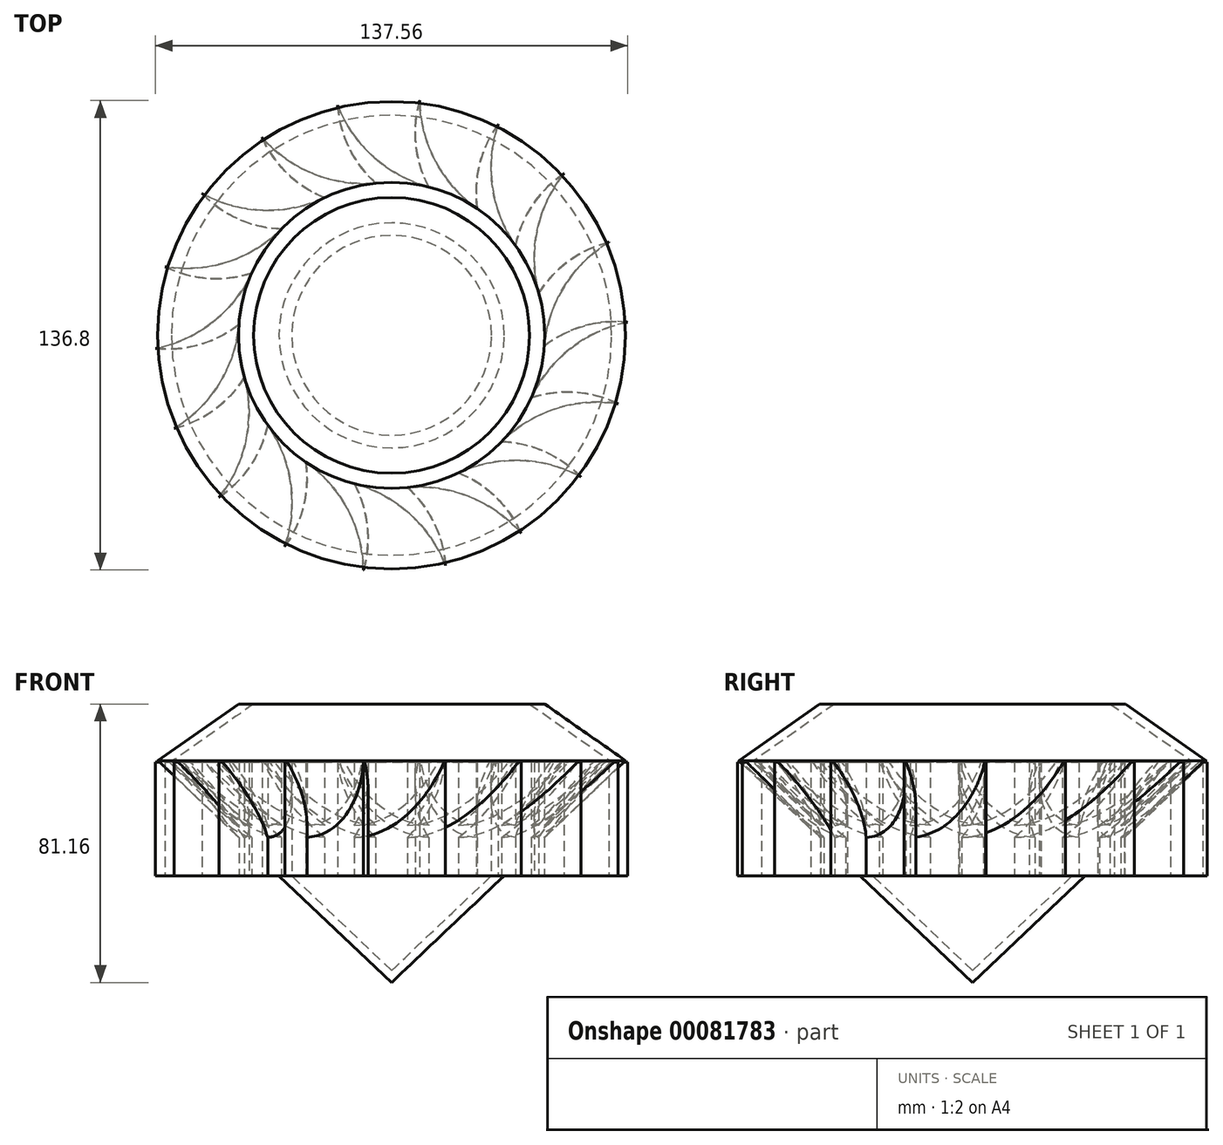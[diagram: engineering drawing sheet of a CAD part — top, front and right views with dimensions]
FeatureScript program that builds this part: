
annotation { "Feature Type Name" : "Feature", "Feature Type Description" : "" }
export const myFeature = defineFeature(function(context is Context, id is Id, definition is map)
    precondition{}
    {
        {
            var Q0;
            Q0=qCreatedBy(makeId("Front.planeOp"),FACE);
            var sketch = newSketch(context, id + "F0", { "sketchPlane" : qUnion([Q0])});
            skLineSegment(sketch, "E0", {"start": v(0, -47.69) * mm, "end": v(-68.1, 16.93) * mm});
            skLineSegment(sketch, "E1", {"start": v(-68.1, 16.93) * mm, "end": v(-44.59, 33.47) * mm});
            skLineSegment(sketch, "E2", {"start": v(-44.59, 33.47) * mm, "end": v(0, 33.47) * mm});
            skLineSegment(sketch, "E3", {"start": v(-68.1, 16.93) * mm, "end": v(0, 16.93) * mm});
            skLineSegment(sketch, "E4.MirrorCS", {"start": v(68.1, 16.93) * mm, "end": v(0, 16.93) * mm});
            skLineSegment(sketch, "E5.MirrorCS", {"start": v(44.59, 33.47) * mm, "end": v(0, 33.47) * mm});
            skLineSegment(sketch, "E6.MirrorCS", {"start": v(68.1, 16.93) * mm, "end": v(44.59, 33.47) * mm});
            skLineSegment(sketch, "E7.MirrorCS", {"start": v(0, -47.69) * mm, "end": v(68.1, 16.93) * mm});
            skLineSegment(sketch, "E8", {"start": v(0, 33.47) * mm, "end": v(0, -50.76) * mm});
            skSolve(sketch);
        }
        {
            var Q0;
            Q0=makeQuery(id+"F0.imprint","IMPRINT",FACE,{"disambiguationData":[TD([[makeQuery(id+"F0.imprint","IMPRINT",EDGE,{"derivedFrom":sQuery(id+"F0.wireOp",EDGE,"E1")}),-1.0]])]});
            var Q1;
            {var subQ0=sQuery(id+"F0.wireOp",EDGE,"E0");Q1=makeQuery(id+"F0.imprint","IMPRINT",FACE,{"disambiguationData":[TD([[makeQuery(id+"F0.imprint","IMPRINT",EDGE,{"derivedFrom":subQ0}),-1.0]])]});}
            var Q2;
            Q2=sQuery(id+"F0.wireOp",EDGE,"E8");
            revolve(context, id + "F1", {"entities" : qUnion([Q0, Q1]), "axis" : qUnion([Q2]), "revolveType" : RevolveType.FULL});
        }
        {
            var Q0;
            Q0=makeQuery(id+"F1.opRevolve","SWEPT_FACE",FACE,{"disambiguationData":[OSD([sQuery(id+"F0.wireOp",EDGE,"E2")])]});
            var Q1;
            Q1=makeQuery(id+"F1.opRevolve","SWEPT_BODY",BODY,{"disambiguationData":[OSD([sQuery(id+"F0.wireOp",EDGE,"E0"),sQuery(id+"F0.wireOp",EDGE,"E1"),sQuery(id+"F0.wireOp",EDGE,"E2"),sQuery(id+"F0.wireOp",EDGE,"E8")])]});
            shell(context, id + "F2", {"entities" : qUnion([Q0]), "parts" : qUnion([Q1]), "thickness" : 2.54 * mm});
        }
        {
            var Q0;
            Q0=qCreatedBy(makeId("Top.planeOp"),FACE);
            var sketch = newSketch(context, id + "F3", { "sketchPlane" : qUnion([Q0])});
            skLineSegment(sketch, "E9", {"start": v(0, 40.18) * mm, "end": v(-4.62, 44.33) * mm});
            skLineSegment(sketch, "E10.1.0", {"start": v(-13.74, 37.76) * mm, "end": v(-19.5, 40.08) * mm});
            skLineSegment(sketch, "E10.2.0", {"start": v(-25.83, 30.78) * mm, "end": v(-32.03, 31) * mm});
            skPoint(sketch, "E10.center", {"position": v(0, 0) * mm});
            skLineSegment(sketch, "E11.2.3.0", {"start": v(-34.8, 20.09) * mm, "end": v(-40.7, 18.17) * mm});
            skLineSegment(sketch, "E11.2.4.0", {"start": v(-39.57, 6.98) * mm, "end": v(-44.46, 3.15) * mm});
            skLineSegment(sketch, "E11.2.5.0", {"start": v(-39.57, -6.98) * mm, "end": v(-42.86, -12.25) * mm});
            skLineSegment(sketch, "E11.2.6.0", {"start": v(-34.8, -20.09) * mm, "end": v(-36.08, -26.16) * mm});
            skLineSegment(sketch, "E11.2.7.0", {"start": v(-25.83, -30.78) * mm, "end": v(-24.96, -36.93) * mm});
            skLineSegment(sketch, "E11.2.8.0", {"start": v(-13.74, -37.76) * mm, "end": v(-10.82, -43.24) * mm});
            skLineSegment(sketch, "E11.2.9.0", {"start": v(0, -40.18) * mm, "end": v(4.62, -44.33) * mm});
            skLineSegment(sketch, "E11.2.10.0", {"start": v(13.74, -37.76) * mm, "end": v(19.5, -40.08) * mm});
            skLineSegment(sketch, "E11.2.11.0", {"start": v(25.83, -30.78) * mm, "end": v(32.03, -31) * mm});
            skLineSegment(sketch, "E11.2.12.0", {"start": v(34.8, -20.09) * mm, "end": v(40.7, -18.17) * mm});
            skLineSegment(sketch, "E11.2.13.0", {"start": v(39.57, -6.98) * mm, "end": v(44.46, -3.15) * mm});
            skLineSegment(sketch, "E11.2.14.0", {"start": v(39.57, 6.98) * mm, "end": v(42.86, 12.25) * mm});
            skLineSegment(sketch, "E11.2.15.0", {"start": v(34.8, 20.09) * mm, "end": v(36.08, 26.16) * mm});
            skLineSegment(sketch, "E11.2.16.0", {"start": v(25.83, 30.78) * mm, "end": v(24.96, 36.93) * mm});
            skLineSegment(sketch, "E11.2.17.0", {"start": v(13.74, 37.76) * mm, "end": v(10.82, 43.24) * mm});
            skArc(sketch, "E12", {"start": v(-37.7, 57.65) * mm, "mid": v(-22.75, 47.05) * mm, "end": v(-4.62, 44.33) * mm});
            skArc(sketch, "E13", {"start": v(-37.7, 57.65) * mm, "mid": v(-30.31, 47.1) * mm, "end": v(-19.5, 40.08) * mm});
            skArc(sketch, "E14.1.0", {"start": v(-55.15, 41.27) * mm, "mid": v(-44.6, 33.88) * mm, "end": v(-32.03, 31) * mm});
            skArc(sketch, "E14.1.1", {"start": v(-55.15, 41.27) * mm, "mid": v(-37.47, 36.43) * mm, "end": v(-19.5, 40.08) * mm});
            skArc(sketch, "E14.2.0", {"start": v(-65.94, 19.92) * mm, "mid": v(-53.5, 16.59) * mm, "end": v(-40.7, 18.17) * mm});
            skArc(sketch, "E14.2.1", {"start": v(-65.94, 19.92) * mm, "mid": v(-47.67, 21.42) * mm, "end": v(-32.03, 31) * mm});
            skArc(sketch, "E15.2.3.0", {"start": v(-68.78, -3.83) * mm, "mid": v(-55.94, -2.7) * mm, "end": v(-44.46, 3.15) * mm});
            skArc(sketch, "E15.4.3.0", {"start": v(-68.78, -3.83) * mm, "mid": v(-52.12, 3.83) * mm, "end": v(-40.7, 18.17) * mm});
            skArc(sketch, "E15.2.4.0", {"start": v(-63.32, -27.12) * mm, "mid": v(-51.64, -21.68) * mm, "end": v(-42.86, -12.25) * mm});
            skArc(sketch, "E15.4.4.0", {"start": v(-63.32, -27.12) * mm, "mid": v(-50.29, -14.23) * mm, "end": v(-44.46, 3.15) * mm});
            skArc(sketch, "E15.2.5.0", {"start": v(-50.22, -47.14) * mm, "mid": v(-41.11, -38.03) * mm, "end": v(-36.08, -26.16) * mm});
            skArc(sketch, "E15.4.5.0", {"start": v(-50.22, -47.14) * mm, "mid": v(-42.39, -30.57) * mm, "end": v(-42.86, -12.25) * mm});
            skArc(sketch, "E15.2.6.0", {"start": v(-31.07, -61.48) * mm, "mid": v(-25.62, -49.8) * mm, "end": v(-24.96, -36.93) * mm});
            skArc(sketch, "E15.4.6.0", {"start": v(-31.07, -61.48) * mm, "mid": v(-29.37, -43.22) * mm, "end": v(-36.08, -26.16) * mm});
            skArc(sketch, "E15.2.7.0", {"start": v(-8.17, -68.4) * mm, "mid": v(-7.05, -55.56) * mm, "end": v(-10.82, -43.24) * mm});
            skArc(sketch, "E15.4.7.0", {"start": v(-8.17, -68.4) * mm, "mid": v(-12.82, -50.66) * mm, "end": v(-24.96, -36.93) * mm});
            skArc(sketch, "E15.2.8.0", {"start": v(15.72, -67.07) * mm, "mid": v(12.38, -54.62) * mm, "end": v(4.62, -44.33) * mm});
            skArc(sketch, "E15.4.8.0", {"start": v(15.72, -67.07) * mm, "mid": v(5.28, -52) * mm, "end": v(-10.82, -43.24) * mm});
            skArc(sketch, "E15.2.9.0", {"start": v(37.7, -57.65) * mm, "mid": v(30.31, -47.1) * mm, "end": v(19.5, -40.08) * mm});
            skArc(sketch, "E15.4.9.0", {"start": v(37.7, -57.65) * mm, "mid": v(22.75, -47.05) * mm, "end": v(4.62, -44.33) * mm});
            skArc(sketch, "E15.2.10.0", {"start": v(55.15, -41.27) * mm, "mid": v(44.6, -33.88) * mm, "end": v(32.03, -31) * mm});
            skArc(sketch, "E15.4.10.0", {"start": v(55.15, -41.27) * mm, "mid": v(37.47, -36.43) * mm, "end": v(19.5, -40.08) * mm});
            skArc(sketch, "E15.2.11.0", {"start": v(65.94, -19.92) * mm, "mid": v(53.5, -16.59) * mm, "end": v(40.7, -18.17) * mm});
            skArc(sketch, "E15.4.11.0", {"start": v(65.94, -19.92) * mm, "mid": v(47.67, -21.42) * mm, "end": v(32.03, -31) * mm});
            skArc(sketch, "E15.2.12.0", {"start": v(68.78, 3.83) * mm, "mid": v(55.94, 2.7) * mm, "end": v(44.46, -3.15) * mm});
            skArc(sketch, "E15.4.12.0", {"start": v(68.78, 3.83) * mm, "mid": v(52.12, -3.83) * mm, "end": v(40.7, -18.17) * mm});
            skArc(sketch, "E15.2.13.0", {"start": v(63.32, 27.12) * mm, "mid": v(51.64, 21.68) * mm, "end": v(42.86, 12.25) * mm});
            skArc(sketch, "E15.4.13.0", {"start": v(63.32, 27.12) * mm, "mid": v(50.29, 14.23) * mm, "end": v(44.46, -3.15) * mm});
            skArc(sketch, "E15.2.14.0", {"start": v(50.22, 47.14) * mm, "mid": v(41.11, 38.03) * mm, "end": v(36.08, 26.16) * mm});
            skArc(sketch, "E15.4.14.0", {"start": v(50.22, 47.14) * mm, "mid": v(42.39, 30.57) * mm, "end": v(42.86, 12.25) * mm});
            skArc(sketch, "E15.2.15.0", {"start": v(31.07, 61.48) * mm, "mid": v(25.62, 49.8) * mm, "end": v(24.96, 36.93) * mm});
            skArc(sketch, "E15.4.15.0", {"start": v(31.07, 61.48) * mm, "mid": v(29.37, 43.22) * mm, "end": v(36.08, 26.16) * mm});
            skArc(sketch, "E15.2.16.0", {"start": v(8.17, 68.4) * mm, "mid": v(7.05, 55.56) * mm, "end": v(10.82, 43.24) * mm});
            skArc(sketch, "E15.4.16.0", {"start": v(8.17, 68.4) * mm, "mid": v(12.82, 50.66) * mm, "end": v(24.96, 36.93) * mm});
            skArc(sketch, "E15.2.17.0", {"start": v(-15.72, 67.07) * mm, "mid": v(-12.38, 54.62) * mm, "end": v(-4.62, 44.33) * mm});
            skArc(sketch, "E15.4.17.0", {"start": v(-15.72, 67.07) * mm, "mid": v(-5.28, 52) * mm, "end": v(10.82, 43.24) * mm});
            skSolve(sketch);
        }
        {
            var Q0;
            Q0=makeQuery(id+"F3.imprint","IMPRINT",FACE,{"disambiguationData":[TD([[makeQuery(id+"F3.imprint","IMPRINT",EDGE,{"derivedFrom":sQuery(id+"F3.wireOp",EDGE,"E12")}),-1.0]])]});
            extrude(context, id + "F4", {"entities" : qUnion([Q0]), "operationType" : NewBodyOperationType.ADD, "endBound" : BoundingType.SYMMETRIC, "depth" : 33.16 * mm});
        }
    });
